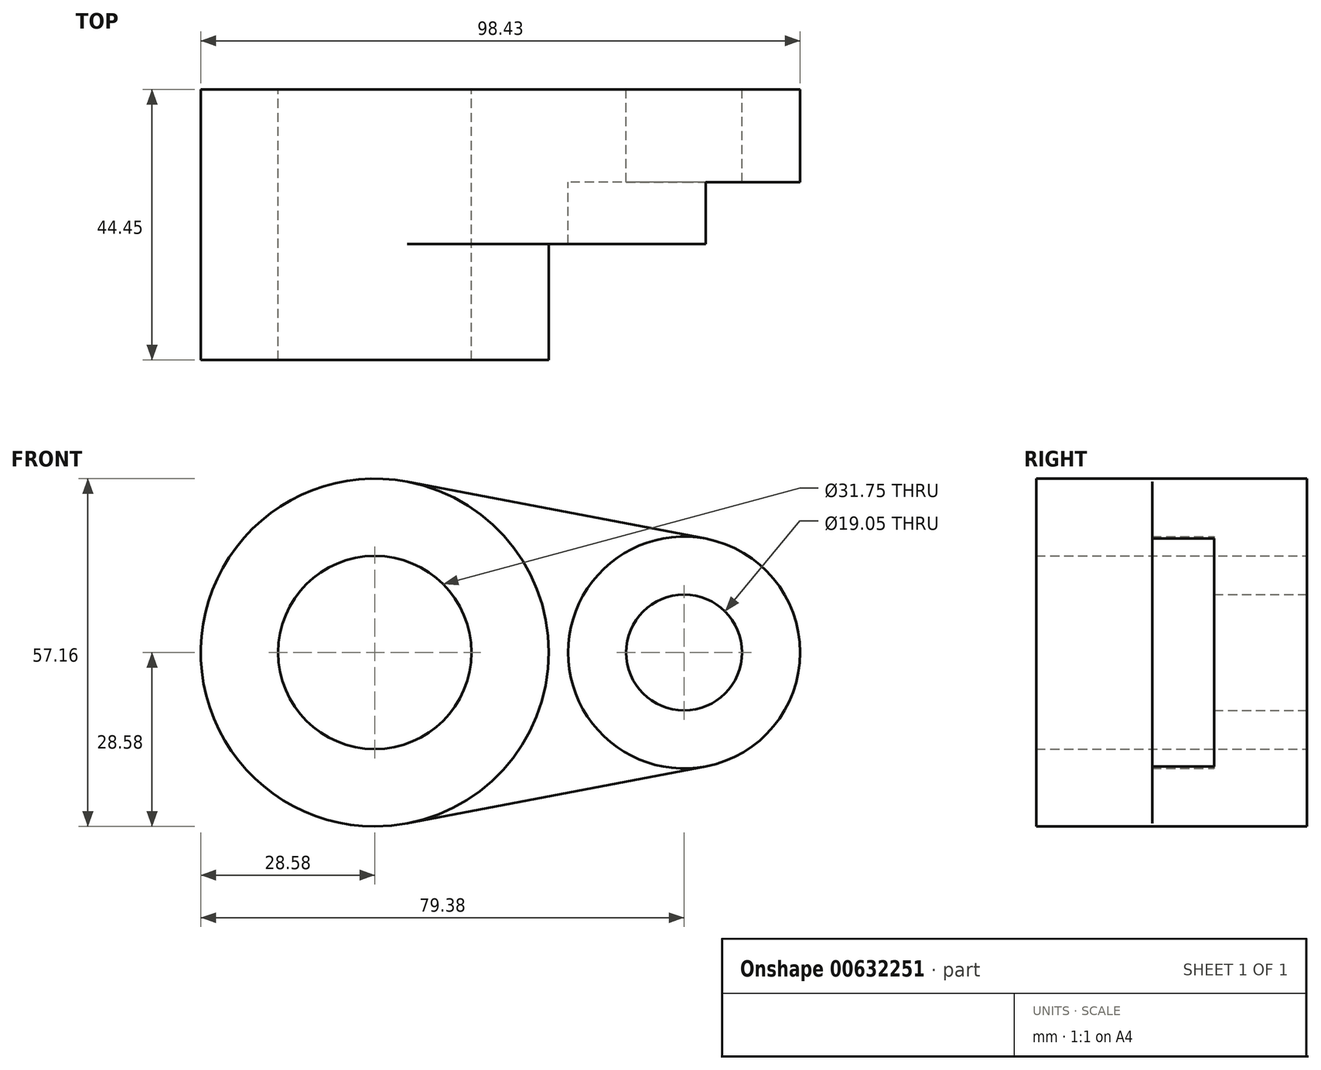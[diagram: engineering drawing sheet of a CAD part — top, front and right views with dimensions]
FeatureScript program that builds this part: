
annotation { "Feature Type Name" : "Feature", "Feature Type Description" : "" }
export const myFeature = defineFeature(function(context is Context, id is Id, definition is map)
    precondition{}
    {
        {
            var Q0;
            Q0=qCreatedBy(makeId("Front.planeOp"),FACE);
            var sketch = newSketch(context, id + "F0", { "sketchPlane" : qUnion([Q0])});
            skCircle(sketch, "E0", {"center": v(50.8, 0) * mm, "radius": 19.05 * mm});
            skCircle(sketch, "E1", {"center": v(0, 0) * mm, "radius": 28.58 * mm});
            skLineSegment(sketch, "E2", {"start": v(5.36, 28.07) * mm, "end": v(54.37, 18.71) * mm});
            skLineSegment(sketch, "E3", {"start": v(5.36, -28.07) * mm, "end": v(54.37, -18.71) * mm});
            skCircle(sketch, "E4", {"center": v(0, 0) * mm, "radius": 15.88 * mm});
            skCircle(sketch, "E5", {"center": v(50.8, 0) * mm, "radius": 9.53 * mm});
            skSolve(sketch);
        }
        {
            var Q0;
            Q0=makeQuery(id+"F0.imprint","IMPRINT",FACE,{"disambiguationData":[TD([[makeQuery(id+"F0.imprint","IMPRINT",EDGE,{"derivedFrom":sQuery(id+"F0.wireOp",EDGE,"E4")}),-1.0]])]});
            extrude(context, id + "F1", {"entities" : qUnion([Q0]), "depth" : 44.45 * mm, "offsetDistance" : 25.4 * mm});
        }
        {
            var Q0;
            {var subQ0=sQuery(id+"F0.wireOp",EDGE,"E2");Q0=makeQuery(id+"F0.imprint","IMPRINT",FACE,{"disambiguationData":[TD([[makeQuery(id+"F0.imprint","IMPRINT",EDGE,{"derivedFrom":subQ0}),-1.0]])]});}
            extrude(context, id + "F2", {"entities" : qUnion([Q0]), "operationType" : NewBodyOperationType.ADD, "depth" : 25.4 * mm, "offsetDistance" : 25.4 * mm});
        }
        {
            var Q0;
            Q0=makeQuery(id+"F0.imprint","IMPRINT",FACE,{"disambiguationData":[TD([[makeQuery(id+"F0.imprint","IMPRINT",EDGE,{"derivedFrom":sQuery(id+"F0.wireOp",EDGE,"E5")}),-1.0]])]});
            extrude(context, id + "F3", {"entities" : qUnion([Q0]), "operationType" : NewBodyOperationType.ADD, "depth" : 15.24 * mm, "offsetDistance" : 25.4 * mm});
        }
    });
